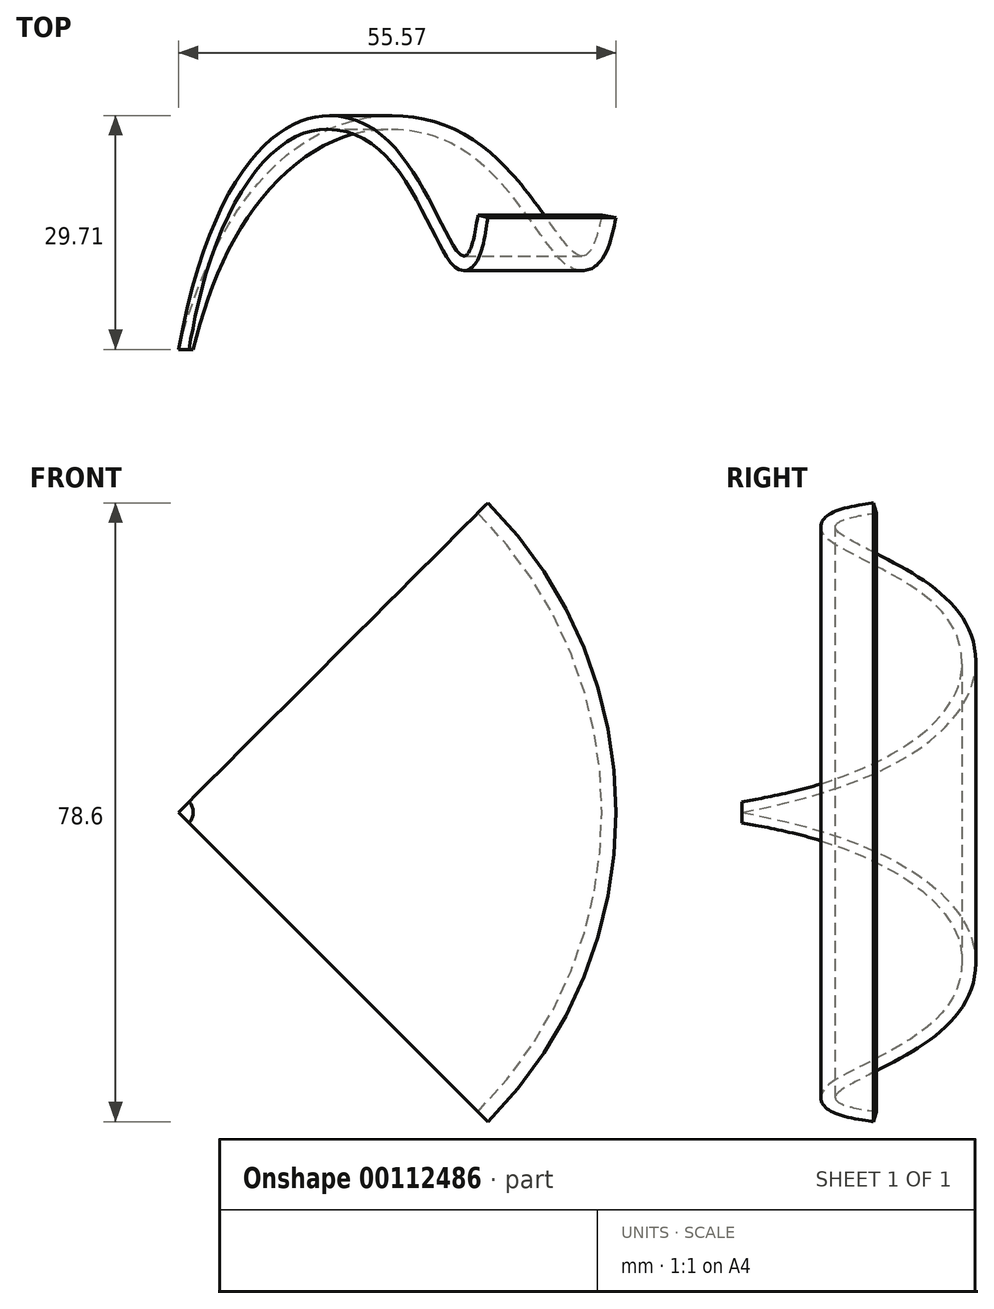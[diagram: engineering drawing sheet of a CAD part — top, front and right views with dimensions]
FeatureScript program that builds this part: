
annotation { "Feature Type Name" : "Feature", "Feature Type Description" : "" }
export const myFeature = defineFeature(function(context is Context, id is Id, definition is map)
    precondition{}
    {
        {
            var Q0;
            Q0=qCreatedBy(makeId("Top.planeOp"),FACE);
            var sketch = newSketch(context, id + "F0", { "sketchPlane" : qUnion([Q0])});
            skPoint(sketch, "E0", {"position": v(0, 0) * mm});
            skPoint(sketch, "E1", {"position": v(35, 28) * mm});
            skPoint(sketch, "E2", {"position": v(49, 13.66) * mm});
            skPoint(sketch, "E3", {"position": v(53.78, 17.07) * mm});
            skFitSpline(sketch, "E4", {"points": [v(0, 0) * mm, v(35, 28) * mm, v(49, 13.66) * mm, v(53.78, 17.07) * mm], "startDerivative": vector(46.02, 175.73) * mm, "endDerivative": vector(22.83, 117.8) * mm});
            skFitSpline(sketch, "E5.0", {"points": [v(1.77, -0.46) * mm, v(2.7, 3.12) * mm, v(4.88, 9.47) * mm, v(8.8, 16.74) * mm, v(13.14, 22) * mm, v(17.7, 25.46) * mm, v(22.3, 27.4) * mm, v(26.03, 27.95) * mm, v(28.89, 27.84) * mm, v(30.94, 27.5) * mm, v(32.88, 26.94) * mm, v(34.68, 26.17) * mm, v(36.34, 25.22) * mm, v(37.88, 24.1) * mm, v(39.32, 22.85) * mm, v(40.66, 21.49) * mm, v(41.92, 20.05) * mm, v(43.1, 18.57) * mm, v(44.2, 17.08) * mm, v(45.27, 15.62) * mm, v(46.11, 14.44) * mm, v(46.78, 13.53) * mm, v(47.28, 12.88) * mm, v(47.78, 12.26) * mm, v(48.3, 11.64) * mm, v(48.88, 11.06) * mm, v(49.45, 10.61) * mm, v(50.02, 10.3) * mm, v(50.52, 10.12) * mm, v(51.1, 10.02) * mm, v(51.74, 10.05) * mm, v(52.37, 10.24) * mm, v(52.92, 10.55) * mm, v(53.36, 10.94) * mm, v(53.85, 11.52) * mm, v(54.32, 12.33) * mm, v(54.78, 13.5) * mm, v(55.2, 14.92) * mm, v(55.45, 16.08) * mm, v(55.57, 16.73) * mm]});
            skLineSegment(sketch, "E6", {"start": v(53.78, 17.07) * mm, "end": v(55.57, 16.73) * mm});
            skLineSegment(sketch, "E7", {"start": v(1.9, 0) * mm, "end": v(0, 0) * mm});
            skLineSegment(sketch, "E8", {"start": v(0, 0) * mm, "end": v(0, 40.65) * mm});
            skSolve(sketch);
        }
        {
            var Q0;
            Q0=makeQuery(id+"F0.imprint","IMPRINT",FACE,{"disambiguationData":[TD([[makeQuery(id+"F0.imprint","IMPRINT",EDGE,{"derivedFrom":sQuery(id+"F0.wireOp",EDGE,"E4")}),-1.0]])]});
            var Q1;
            Q1=sQuery(id+"F0.wireOp",EDGE,"E8");
            revolve(context, id + "F1", {"entities" : qUnion([Q0]), "axis" : qUnion([Q1]), "revolveType" : RevolveType.SYMMETRIC, "angle" : 90 * degree});
        }
    });
